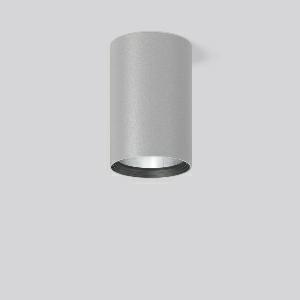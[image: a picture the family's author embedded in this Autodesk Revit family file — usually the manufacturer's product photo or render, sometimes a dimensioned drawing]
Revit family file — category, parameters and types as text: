
# Revit family: heledon_maxi_a_931233_004_e960
name_source: partatom
category: Lighting Fixtures
units: mm (PartAtom-declared; Revit-internal decimal feet)

## family parameters
Cut with Voids When Loaded = No
Host = Face
Light Source = No
Part Type = Normal
Room Calculation Point = No
Round Connector Dimension = Use Diameter
Shared = No

## types (1)
- HELEDON maxi A (1 x LED Modul 932 fresh meat, 2050 lm, 3200)
    Apparent Load = 33 VA
    Approval mark = CE
    CIE Flux Codes = 96 100 100 100 100
    Color Rendering = 90
    Color Temperature = 3200
    Default Elevation = 1800 mm
    Description = Series: HELEDON maxi
Cylindrical surface-mounted downlight. Housing: die-cast aluminium, powder-coated. Internal ceiling frame polycarbonate with bayonet mounting. Black plastic ring and recessed LED to prevent glare from the side. Optical assembly with reflector made of MIRO-Silver with 98% total light reflection for outstanding efficiency - can be changed without tools. Special LED for illumination of meat included. Suitable for Ceiling mounting. Easy installation with a separate ceiling frame with bayonet mounting and plug connection. Driver integrated. Connected via plug-in connector. High quality converter without flickering and stroboscopic effect. The following accessories can be mounted without use of tools: interchangeable lenses, decorative glasses, honeycomb louvre, clear and frosted diffusers, white interchangeable plastic ring. 
Colour: silver
Diameter: 123 mm
Height: 183 mm
Lamp: LED
Socket: without socket
Colour temperature: fresh meat
System power: 33 W
Rated luminous flux: 2050 lm
Luminous efficiency: 62 lm/W
Control gear: Regulated power supply
Protection class: I
Type of protection: IP 20
    Height = 183 mm
    Lamp = 1 x LED Modul 932 fresh meat
    Lamp Light Flux = 2050 lm
    Lamp count = 1
    Length = 123 mm
    Lifetime = 50000 h
    Luminous efficacy = 62 lm/W
    Manufacturer = RZB
    ModVariant = No
    Model = 931233.004
    Mounting Place = Ceiling
    Mounting Type = Surface mounted
    Number of Poles = 1
    OnlyDefault = Yes
    Power Factor = 1
    Product Name = HELEDON maxi A
    Product group = Surface mounted downlights
    ProductGroupID = 302
    Protection Class = Protection class I
    Protection Degree = IP 20
    RLX_Detail_Level = 1
    RLX_Emergency_Light_Flux = 0 lm
    RLX_Emergency_Type = 0
    RLX_Emergency_Type_DB = No
    RlxData = <blob elided: 99577 chars, md5=a88ddb3c>
    Socket = socket
    Standby Power = 0 W
    System Light Flux = 2050 lm
    System Power = 33 W
    Type Comments = Product without accessories
    Type Image = 931192.004.jpg
    URL = http://relux.com
    VarID = ---
    Voltage = 230 V
    Voltage Range = 220-240 V
    Weight = 0.00 kg
    Width = 0 mm  [stored 0 ft]

note: [stored X ft] marks values corroborated as IEEE doubles in the binary element streams (Revit-internal decimal feet)

## geometry (parser evidence)
native form markers: Blend x4, Sweep x10
no freeform markers — native parametric forms only
